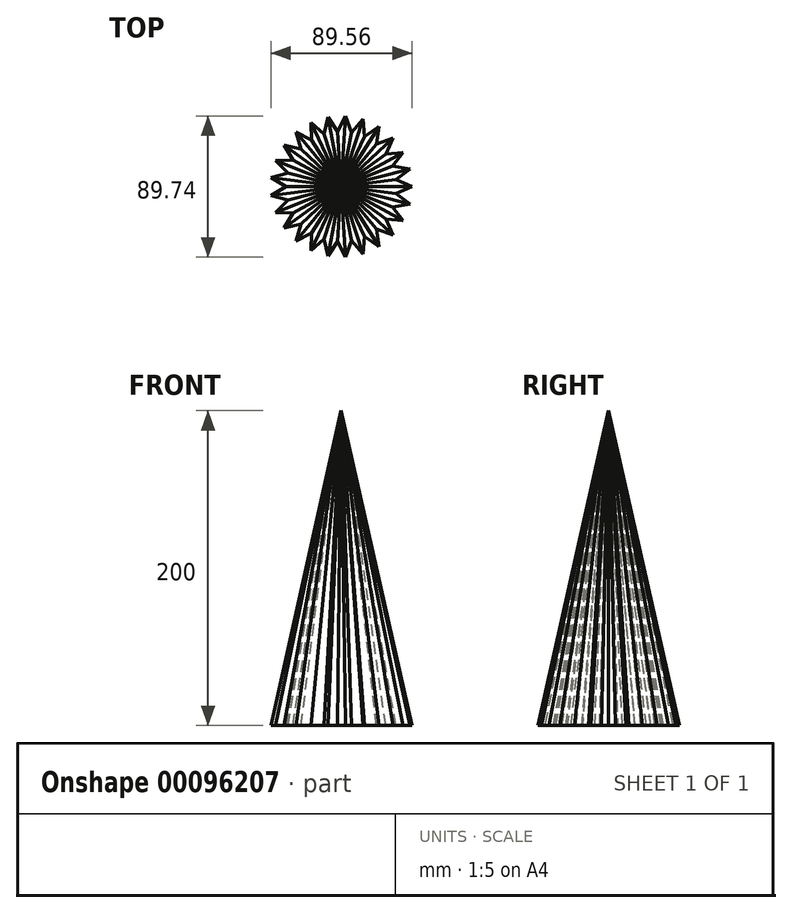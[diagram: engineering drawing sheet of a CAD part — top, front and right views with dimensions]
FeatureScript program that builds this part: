
annotation { "Feature Type Name" : "Feature", "Feature Type Description" : "" }
export const myFeature = defineFeature(function(context is Context, id is Id, definition is map)
    precondition{}
    {
        {
            var Q0;
            Q0=qCreatedBy(makeId("Front.planeOp"),FACE);
            var sketch = newSketch(context, id + "F0", { "sketchPlane" : qUnion([Q0])});
            skLineSegment(sketch, "E0", {"start": v(0, 0) * mm, "end": v(0, 200) * mm});
            skLineSegment(sketch, "E1", {"start": v(0, 200) * mm, "end": v(-45, 0) * mm});
            skLineSegment(sketch, "E2", {"start": v(-45, 0) * mm, "end": v(0, 0) * mm});
            skSolve(sketch);
        }
        {
            var Q0;
            Q0=makeQuery(id+"F0.imprint","IMPRINT",FACE,{"disambiguationData":[TD([[makeQuery(id+"F0.imprint","IMPRINT",EDGE,{"derivedFrom":sQuery(id+"F0.wireOp",EDGE,"E0")}),1.0]])]});
            var Q1;
            Q1=sQuery(id+"F0.wireOp",EDGE,"E0");
            revolve(context, id + "F1", {"entities" : qUnion([Q0]), "axis" : qUnion([Q1]), "revolveType" : RevolveType.FULL});
        }
        {
            var Q0;
            Q0=sQuery(id+"F0.wireOp",EDGE,"E2");
            cPlane(context, id + "F2", {"entities" : qUnion([Q0]), "cplaneType" : CPlaneType.LINE_ANGLE, "offset" : 150 * mm, "angle" : 12.68 * degree, "width" : 150 * mm, "height" : 150 * mm});
        }
        {
            var Q0;
            Q0=qCreatedBy(id+"F2.planeOp",FACE);
            cPlane(context, id + "F3", {"entities" : qUnion([Q0]), "cplaneType" : CPlaneType.OFFSET, "offset" : 45 * mm, "width" : 150 * mm, "height" : 150 * mm});
        }
        {
            var Q0;
            Q0=qCreatedBy(id+"F3.planeOp",FACE);
            var sketch = newSketch(context, id + "F4", { "sketchPlane" : qUnion([Q0])});
            skLineSegment(sketch, "E3", {"start": v(0, 195.12) * mm, "end": v(0, -9.88) * mm});
            skLineSegment(sketch, "E4", {"start": v(-46.73, -9.88) * mm, "end": v(43.27, -9.88) * mm});
            skSolve(sketch);
        }
        {
            var Q0;
            Q0=makeQuery(id+"F1.opRevolve","SWEPT_FACE",FACE,{"disambiguationData":[OSD([sQuery(id+"F0.wireOp",EDGE,"E2")])]});
            var sketch = newSketch(context, id + "F5", { "sketchPlane" : qUnion([Q0])});
            skLineSegment(sketch, "E5", {"start": v(-35, 0) * mm, "end": v(-44.64, 5.66) * mm});
            skLineSegment(sketch, "E6", {"start": v(-35, 0) * mm, "end": v(-44.64, -5.66) * mm});
            skArc(sketch, "E7.0", {"start": v(-44.64, 5.66) * mm, "mid": v(-45, 0) * mm, "end": v(-44.64, -5.66) * mm});
            skSolve(sketch);
        }
        {
            var Q0;
            Q0=qCreatedBy(makeId("Front.planeOp"),FACE);
            var sketch = newSketch(context, id + "F6", { "sketchPlane" : qUnion([Q0])});
            skLineSegment(sketch, "E8", {"start": v(-35, 0) * mm, "end": v(2.92, 216.7) * mm});
            skSolve(sketch);
        }
        {
            var Q0;
            Q0=makeQuery(id+"F5.imprint","IMPRINT",FACE,{"disambiguationData":[TD([[makeQuery(id+"F5.imprint","IMPRINT",EDGE,{"derivedFrom":sQuery(id+"F5.wireOp",EDGE,"E5")}),1.0]])]});
            var Q1;
            Q1=sQuery(id+"F6.wireOp",EDGE,"E8");
            sweep(context, id + "F7", {"profiles" : qUnion([Q0]), "path" : qUnion([Q1])});
        }
        {
            var Q0;
            Q0=makeQuery(id+"F7.opSweep","SWEPT_BODY",BODY,{"disambiguationData":[OSD([sQuery(id+"F5.wireOp",EDGE,"E5"),sQuery(id+"F5.wireOp",EDGE,"E6"),sQuery(id+"F5.wireOp",EDGE,"E7.0"),sQuery(id+"F6.wireOp",EDGE,"E8")])]});
            var Q1;
            Q1=makeQuery(id+"F1.opRevolve","SWEPT_EDGE",EDGE,{"disambiguationData":[OSD([sQuery(id+"F0.wireOp",EDGE,"E1"),sQuery(id+"F0.wireOp",EDGE,"E2")])]});
            circularPattern(context, id + "F8", {"entities" : qUnion([Q0]), "axis" : qUnion([Q1]), "angle" : 360 * degree, "instanceCount" : 25, "equalSpace" : true});
        }
        {
            var Q0;
            Q0=makeQuery(id+"F7.opSweep","SWEPT_BODY",BODY,{"disambiguationData":[OSD([sQuery(id+"F5.wireOp",EDGE,"E5"),sQuery(id+"F5.wireOp",EDGE,"E6"),sQuery(id+"F5.wireOp",EDGE,"E7.0"),sQuery(id+"F6.wireOp",EDGE,"E8")])]});
            var Q1;
            Q1=makeQuery(id+"F8.opPattern","COPY",BODY,{"derivedFrom":makeQuery(id+"F7.opSweep","SWEPT_BODY",BODY,{"disambiguationData":[OSD([sQuery(id+"F5.wireOp",EDGE,"E5"),sQuery(id+"F5.wireOp",EDGE,"E6"),sQuery(id+"F5.wireOp",EDGE,"E7.0"),sQuery(id+"F6.wireOp",EDGE,"E8")])]}),"instanceName":"1"});
            var Q2;
            Q2=makeQuery(id+"F8.opPattern","COPY",BODY,{"derivedFrom":makeQuery(id+"F7.opSweep","SWEPT_BODY",BODY,{"disambiguationData":[OSD([sQuery(id+"F5.wireOp",EDGE,"E5"),sQuery(id+"F5.wireOp",EDGE,"E6"),sQuery(id+"F5.wireOp",EDGE,"E7.0"),sQuery(id+"F6.wireOp",EDGE,"E8")])]}),"instanceName":"2"});
            var Q3;
            Q3=makeQuery(id+"F8.opPattern","COPY",BODY,{"derivedFrom":makeQuery(id+"F7.opSweep","SWEPT_BODY",BODY,{"disambiguationData":[OSD([sQuery(id+"F5.wireOp",EDGE,"E5"),sQuery(id+"F5.wireOp",EDGE,"E6"),sQuery(id+"F5.wireOp",EDGE,"E7.0"),sQuery(id+"F6.wireOp",EDGE,"E8")])]}),"instanceName":"3"});
            var Q4;
            Q4=makeQuery(id+"F8.opPattern","COPY",BODY,{"derivedFrom":makeQuery(id+"F7.opSweep","SWEPT_BODY",BODY,{"disambiguationData":[OSD([sQuery(id+"F5.wireOp",EDGE,"E5"),sQuery(id+"F5.wireOp",EDGE,"E6"),sQuery(id+"F5.wireOp",EDGE,"E7.0"),sQuery(id+"F6.wireOp",EDGE,"E8")])]}),"instanceName":"6"});
            var Q5;
            Q5=makeQuery(id+"F8.opPattern","COPY",BODY,{"derivedFrom":makeQuery(id+"F7.opSweep","SWEPT_BODY",BODY,{"disambiguationData":[OSD([sQuery(id+"F5.wireOp",EDGE,"E5"),sQuery(id+"F5.wireOp",EDGE,"E6"),sQuery(id+"F5.wireOp",EDGE,"E7.0"),sQuery(id+"F6.wireOp",EDGE,"E8")])]}),"instanceName":"7"});
            var Q6;
            Q6=makeQuery(id+"F8.opPattern","COPY",BODY,{"derivedFrom":makeQuery(id+"F7.opSweep","SWEPT_BODY",BODY,{"disambiguationData":[OSD([sQuery(id+"F5.wireOp",EDGE,"E5"),sQuery(id+"F5.wireOp",EDGE,"E6"),sQuery(id+"F5.wireOp",EDGE,"E7.0"),sQuery(id+"F6.wireOp",EDGE,"E8")])]}),"instanceName":"8"});
            var Q7;
            Q7=makeQuery(id+"F8.opPattern","COPY",BODY,{"derivedFrom":makeQuery(id+"F7.opSweep","SWEPT_BODY",BODY,{"disambiguationData":[OSD([sQuery(id+"F5.wireOp",EDGE,"E5"),sQuery(id+"F5.wireOp",EDGE,"E6"),sQuery(id+"F5.wireOp",EDGE,"E7.0"),sQuery(id+"F6.wireOp",EDGE,"E8")])]}),"instanceName":"9"});
            var Q8;
            Q8=makeQuery(id+"F8.opPattern","COPY",BODY,{"derivedFrom":makeQuery(id+"F7.opSweep","SWEPT_BODY",BODY,{"disambiguationData":[OSD([sQuery(id+"F5.wireOp",EDGE,"E5"),sQuery(id+"F5.wireOp",EDGE,"E6"),sQuery(id+"F5.wireOp",EDGE,"E7.0"),sQuery(id+"F6.wireOp",EDGE,"E8")])]}),"instanceName":"10"});
            var Q9;
            Q9=makeQuery(id+"F8.opPattern","COPY",BODY,{"derivedFrom":makeQuery(id+"F7.opSweep","SWEPT_BODY",BODY,{"disambiguationData":[OSD([sQuery(id+"F5.wireOp",EDGE,"E5"),sQuery(id+"F5.wireOp",EDGE,"E6"),sQuery(id+"F5.wireOp",EDGE,"E7.0"),sQuery(id+"F6.wireOp",EDGE,"E8")])]}),"instanceName":"11"});
            var Q10;
            Q10=makeQuery(id+"F8.opPattern","COPY",BODY,{"derivedFrom":makeQuery(id+"F7.opSweep","SWEPT_BODY",BODY,{"disambiguationData":[OSD([sQuery(id+"F5.wireOp",EDGE,"E5"),sQuery(id+"F5.wireOp",EDGE,"E6"),sQuery(id+"F5.wireOp",EDGE,"E7.0"),sQuery(id+"F6.wireOp",EDGE,"E8")])]}),"instanceName":"12"});
            var Q11;
            Q11=makeQuery(id+"F8.opPattern","COPY",BODY,{"derivedFrom":makeQuery(id+"F7.opSweep","SWEPT_BODY",BODY,{"disambiguationData":[OSD([sQuery(id+"F5.wireOp",EDGE,"E5"),sQuery(id+"F5.wireOp",EDGE,"E6"),sQuery(id+"F5.wireOp",EDGE,"E7.0"),sQuery(id+"F6.wireOp",EDGE,"E8")])]}),"instanceName":"13"});
            var Q12;
            Q12=makeQuery(id+"F8.opPattern","COPY",BODY,{"derivedFrom":makeQuery(id+"F7.opSweep","SWEPT_BODY",BODY,{"disambiguationData":[OSD([sQuery(id+"F5.wireOp",EDGE,"E5"),sQuery(id+"F5.wireOp",EDGE,"E6"),sQuery(id+"F5.wireOp",EDGE,"E7.0"),sQuery(id+"F6.wireOp",EDGE,"E8")])]}),"instanceName":"14"});
            var Q13;
            Q13=makeQuery(id+"F8.opPattern","COPY",BODY,{"derivedFrom":makeQuery(id+"F7.opSweep","SWEPT_BODY",BODY,{"disambiguationData":[OSD([sQuery(id+"F5.wireOp",EDGE,"E5"),sQuery(id+"F5.wireOp",EDGE,"E6"),sQuery(id+"F5.wireOp",EDGE,"E7.0"),sQuery(id+"F6.wireOp",EDGE,"E8")])]}),"instanceName":"15"});
            var Q14;
            Q14=makeQuery(id+"F8.opPattern","COPY",BODY,{"derivedFrom":makeQuery(id+"F7.opSweep","SWEPT_BODY",BODY,{"disambiguationData":[OSD([sQuery(id+"F5.wireOp",EDGE,"E5"),sQuery(id+"F5.wireOp",EDGE,"E6"),sQuery(id+"F5.wireOp",EDGE,"E7.0"),sQuery(id+"F6.wireOp",EDGE,"E8")])]}),"instanceName":"16"});
            var Q15;
            Q15=makeQuery(id+"F8.opPattern","COPY",BODY,{"derivedFrom":makeQuery(id+"F7.opSweep","SWEPT_BODY",BODY,{"disambiguationData":[OSD([sQuery(id+"F5.wireOp",EDGE,"E5"),sQuery(id+"F5.wireOp",EDGE,"E6"),sQuery(id+"F5.wireOp",EDGE,"E7.0"),sQuery(id+"F6.wireOp",EDGE,"E8")])]}),"instanceName":"17"});
            var Q16;
            Q16=makeQuery(id+"F8.opPattern","COPY",BODY,{"derivedFrom":makeQuery(id+"F7.opSweep","SWEPT_BODY",BODY,{"disambiguationData":[OSD([sQuery(id+"F5.wireOp",EDGE,"E5"),sQuery(id+"F5.wireOp",EDGE,"E6"),sQuery(id+"F5.wireOp",EDGE,"E7.0"),sQuery(id+"F6.wireOp",EDGE,"E8")])]}),"instanceName":"18"});
            var Q17;
            Q17=makeQuery(id+"F8.opPattern","COPY",BODY,{"derivedFrom":makeQuery(id+"F7.opSweep","SWEPT_BODY",BODY,{"disambiguationData":[OSD([sQuery(id+"F5.wireOp",EDGE,"E5"),sQuery(id+"F5.wireOp",EDGE,"E6"),sQuery(id+"F5.wireOp",EDGE,"E7.0"),sQuery(id+"F6.wireOp",EDGE,"E8")])]}),"instanceName":"19"});
            var Q18;
            Q18=makeQuery(id+"F8.opPattern","COPY",BODY,{"derivedFrom":makeQuery(id+"F7.opSweep","SWEPT_BODY",BODY,{"disambiguationData":[OSD([sQuery(id+"F5.wireOp",EDGE,"E5"),sQuery(id+"F5.wireOp",EDGE,"E6"),sQuery(id+"F5.wireOp",EDGE,"E7.0"),sQuery(id+"F6.wireOp",EDGE,"E8")])]}),"instanceName":"20"});
            var Q19;
            Q19=makeQuery(id+"F8.opPattern","COPY",BODY,{"derivedFrom":makeQuery(id+"F7.opSweep","SWEPT_BODY",BODY,{"disambiguationData":[OSD([sQuery(id+"F5.wireOp",EDGE,"E5"),sQuery(id+"F5.wireOp",EDGE,"E6"),sQuery(id+"F5.wireOp",EDGE,"E7.0"),sQuery(id+"F6.wireOp",EDGE,"E8")])]}),"instanceName":"21"});
            var Q20;
            Q20=makeQuery(id+"F8.opPattern","COPY",BODY,{"derivedFrom":makeQuery(id+"F7.opSweep","SWEPT_BODY",BODY,{"disambiguationData":[OSD([sQuery(id+"F5.wireOp",EDGE,"E5"),sQuery(id+"F5.wireOp",EDGE,"E6"),sQuery(id+"F5.wireOp",EDGE,"E7.0"),sQuery(id+"F6.wireOp",EDGE,"E8")])]}),"instanceName":"22"});
            var Q21;
            Q21=makeQuery(id+"F8.opPattern","COPY",BODY,{"derivedFrom":makeQuery(id+"F7.opSweep","SWEPT_BODY",BODY,{"disambiguationData":[OSD([sQuery(id+"F5.wireOp",EDGE,"E5"),sQuery(id+"F5.wireOp",EDGE,"E6"),sQuery(id+"F5.wireOp",EDGE,"E7.0"),sQuery(id+"F6.wireOp",EDGE,"E8")])]}),"instanceName":"23"});
            var Q22;
            Q22=makeQuery(id+"F8.opPattern","COPY",BODY,{"derivedFrom":makeQuery(id+"F7.opSweep","SWEPT_BODY",BODY,{"disambiguationData":[OSD([sQuery(id+"F5.wireOp",EDGE,"E5"),sQuery(id+"F5.wireOp",EDGE,"E6"),sQuery(id+"F5.wireOp",EDGE,"E7.0"),sQuery(id+"F6.wireOp",EDGE,"E8")])]}),"instanceName":"24"});
            var Q23;
            Q23=makeQuery(id+"F8.opPattern","COPY",BODY,{"derivedFrom":makeQuery(id+"F7.opSweep","SWEPT_BODY",BODY,{"disambiguationData":[OSD([sQuery(id+"F5.wireOp",EDGE,"E5"),sQuery(id+"F5.wireOp",EDGE,"E6"),sQuery(id+"F5.wireOp",EDGE,"E7.0"),sQuery(id+"F6.wireOp",EDGE,"E8")])]}),"instanceName":"4"});
            var Q24;
            Q24=makeQuery(id+"F8.opPattern","COPY",BODY,{"derivedFrom":makeQuery(id+"F7.opSweep","SWEPT_BODY",BODY,{"disambiguationData":[OSD([sQuery(id+"F5.wireOp",EDGE,"E5"),sQuery(id+"F5.wireOp",EDGE,"E6"),sQuery(id+"F5.wireOp",EDGE,"E7.0"),sQuery(id+"F6.wireOp",EDGE,"E8")])]}),"instanceName":"5"});
            var Q25;
            Q25=makeQuery(id+"F1.opRevolve","SWEPT_BODY",BODY,{"disambiguationData":[OSD([sQuery(id+"F0.wireOp",EDGE,"E0"),sQuery(id+"F0.wireOp",EDGE,"E1"),sQuery(id+"F0.wireOp",EDGE,"E2")])]});
            booleanBodies(context, id + "F9", {"operationType" : BooleanOperationType.SUBTRACTION, "tools" : qUnion([Q0, Q1, Q2, Q3, Q4, Q5, Q6, Q7, Q8, Q9, Q10, Q11, Q12, Q13, Q14, Q15, Q16, Q17, Q18, Q19, Q20, Q21, Q22, Q23, Q24]), "targets" : qUnion([Q25])});
        }
    });
